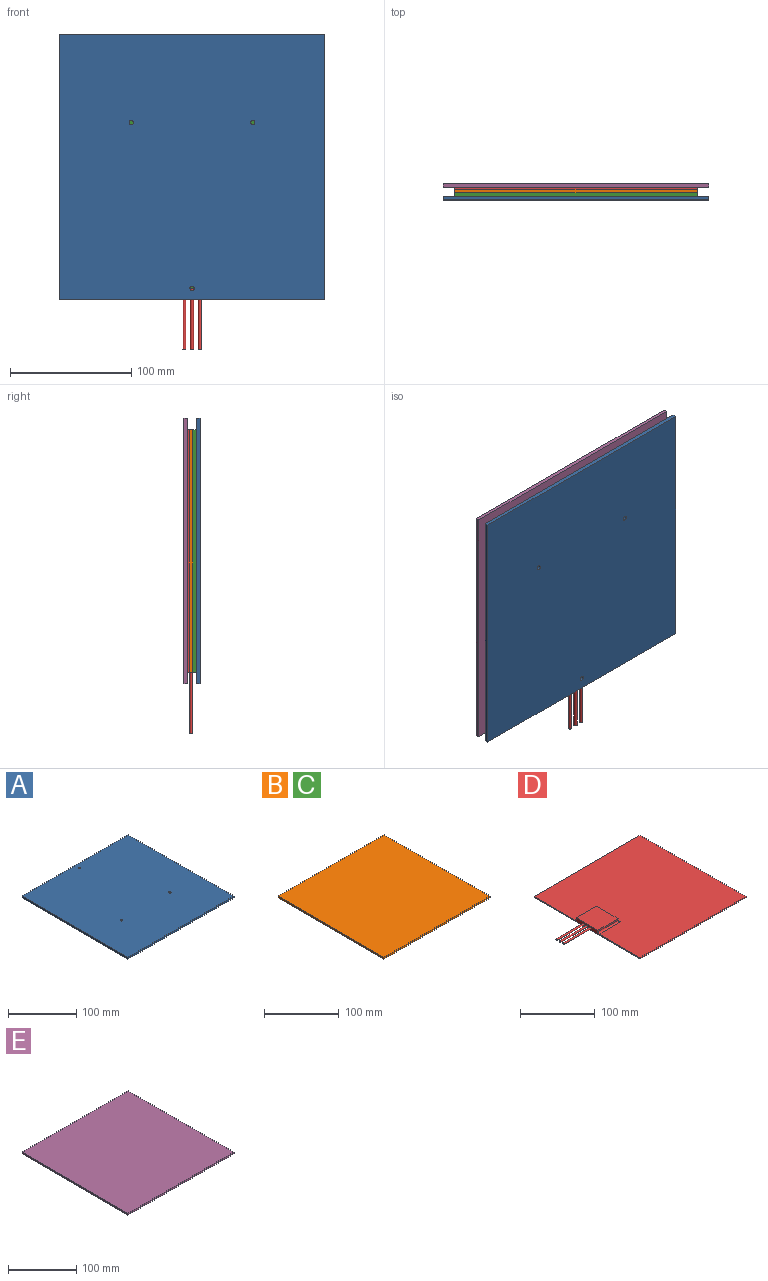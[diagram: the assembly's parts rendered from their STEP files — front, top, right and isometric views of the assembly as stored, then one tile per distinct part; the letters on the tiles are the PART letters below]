
ASSEMBLY  parts=5 mates=6
PART A: 9 faces, bbox 219.1x219.1x3.2 mm
  f0: plane 219.08x3.18mm, normal (0,-1,0), area 695.6mm2, adj f1,f3,f4,f5
  f1: plane 219.08x3.18mm, normal (1,0,0), area 695.6mm2, adj f0,f2,f4,f5
  f2: plane 219.08x3.18mm, normal (0,1,0), area 695.6mm2, adj f1,f3,f4,f5
  f3: plane 219.08x3.18mm, normal (-1,0,0), area 695.6mm2, adj f0,f2,f4,f5
  f4: plane 219.08x219.08mm, normal (0,0,1), area 47964.1mm2, adj f0,f1,f2,f3,f6,f7,f8
  f5: plane 219.08x219.08mm, normal (0,0,-1), area 47964.1mm2, adj f0,f1,f2,f3,f6,f7,f8
  f6: cylinder r=1.78mm len=3.56mm, axis (0,0,1), area 35.5mm2, adj f4,f5
  f7: cylinder r=1.78mm len=3.56mm, axis (0,0,1), area 35.5mm2, adj f4,f5
  f8: cylinder r=1.78mm len=3.56mm, axis (0,0,1), area 35.5mm2, adj f4,f5
PART B: 6 faces, bbox 200x200x2.8 mm
  f0: plane 200.03x2.79mm, normal (0,-1,0), area 558.9mm2, adj f1,f3,f4,f5
  f1: plane 200.03x2.79mm, normal (1,0,0), area 558.9mm2, adj f0,f2,f4,f5
  f2: plane 200.03x2.79mm, normal (0,1,0), area 558.9mm2, adj f1,f3,f4,f5
  f3: plane 200.03x2.79mm, normal (-1,0,0), area 558.9mm2, adj f0,f2,f4,f5
  f4: plane 200.03x200.03mm, normal (0,0,1), area 40010mm2, adj f0,f1,f2,f3
  f5: plane 200.03x200.03mm, normal (0,0,-1), area 40010mm2, adj f0,f1,f2,f3
PART C: same geometry as B
PART D: 19 faces, bbox 250.8x200x6.7 mm
  f0: plane 200.03x200.03mm, normal (0,0,1), area 38126.1mm2, adj f1,f2,f3,f4,f10,f11,f12
  f1: plane 200.03x1.65mm, normal (0,-1,0), area 330.2mm2, adj f0,f2,f4,f5
  f2: plane 200.03x1.65mm, normal (1,0,0), area 330.2mm2, adj f0,f1,f3,f5
  f3: plane 200.03x1.65mm, normal (0,1,0), area 330.2mm2, adj f0,f2,f4,f5
  f4: plane 200.03x6.73mm, normal (-1,0,0), area 527.5mm2, adj f0,f1,f3,f5,f6,f7,f9,f10
  f5: plane 200.03x200.03mm, normal (0,0,-1), area 40010mm2, adj f1,f2,f3,f4
  f6: plane 38.1x2.54mm, normal (0,1,0), area 96.8mm2, adj f4,f8,f9,f10
  f7: plane 38.1x2.54mm, normal (0,-1,0), area 96.8mm2, adj f4,f8,f9,f12
  f8: plane 41.28x2.54mm, normal (1,0,0), area 104.8mm2, adj f6,f7,f9,f11
  f9: plane 41.28x38.1mm, normal (0,0,1), area 1572.6mm2, adj f4,f6,f7,f8
  f10: cylinder r=2.54mm len=40.64mm, axis (-1,0,0), area 155.7mm2, adj f0,f4,f6,f11
  f11: cylinder r=2.54mm len=46.36mm, axis (0,1,0), area 172mm2, adj f0,f8,f10,f12
  f12: cylinder r=2.54mm len=40.64mm, axis (1,0,0), area 155.7mm2, adj f0,f4,f7,f11
  f13: cylinder r=1.27mm len=50.8mm, axis (1,0,0), area 405.4mm2, adj f4,f14
  f14: plane 2.54x2.54mm, normal (-1,0,0), area 5.1mm2, adj f13
  f15: cylinder r=1.27mm len=50.8mm, axis (1,0,0), area 405.4mm2, adj f4,f16
  f16: plane 2.54x2.54mm, normal (-1,0,0), area 5.1mm2, adj f15
  f17: cylinder r=1.27mm len=50.8mm, axis (1,0,0), area 405.4mm2, adj f4,f18
  f18: plane 2.54x2.54mm, normal (-1,0,0), area 5.1mm2, adj f17
PART E: 6 faces, bbox 219.1x219.1x2.9 mm
  f0: plane 219.08x2.92mm, normal (0,-1,0), area 639.9mm2, adj f1,f3,f4,f5
  f1: plane 219.08x2.92mm, normal (1,0,0), area 639.9mm2, adj f0,f2,f4,f5
  f2: plane 219.08x2.92mm, normal (0,1,0), area 639.9mm2, adj f1,f3,f4,f5
  f3: plane 219.08x2.92mm, normal (-1,0,0), area 639.9mm2, adj f0,f2,f4,f5
  f4: plane 219.08x219.08mm, normal (0,0,1), area 47993.9mm2, adj f0,f1,f2,f3
  f5: plane 219.08x219.08mm, normal (0,0,-1), area 47993.9mm2, adj f0,f1,f2,f3
PLACE A rot(axis=(-1,0,0),90deg) t=(250.02,-5.63,-114.13)mm
PLACE B rot(axis=(-1,0,0),90deg) t=(250.02,0.34,-114.13)mm
PLACE C rot(axis=(-1,0,0),90deg) t=(250.02,-2.45,-114.13)mm
PLACE D rot(axis=(0.58,-0.58,0.58),120deg) t=(250.02,4.78,-114.13)mm
PLACE E rot(axis=(0,0.71,-0.71),180deg) t=(250.02,7.71,-114.13)mm fixed
MATE planar C.f4 <-> B.f5  axis (0,1,0) through (250.02,0.34,-114.13)mm
MATE fastened D.f0 <-> B.f4  axis (0,-1,0) through (350.03,3.13,-214.15)mm
MATE fastened B.f5 <-> C.f4  axis (0,-1,0) through (350.03,0.34,-14.12)mm
MATE fastened D.f5 <-> E.f4  axis (0,1,0) through (250.02,4.78,-114.13)mm
MATE planar A.f4 <-> C.f5  axis (0,1,0) through (250.02,-2.45,-114.13)mm
MATE fastened C.f5 <-> A.f4  axis (0,1,0) through (350.03,-2.45,-14.12)mm
